FCSTD DOCUMENT  (FreeCAD 0.15R4403 (Git))
Label: logo
License: CC-BY 3.0
LicenseURL: http://creativecommons.org/licenses/by/3.0/
objects: Sketcher::SketchObject×1
note: 1 computed .brp shape members not serialized (recipe doc carries the construction recipe); baked Part::Feature solids carry a one-line shape summary decoded from their .brp

FEATURE [Sketcher::SketchObject] Sketch
  sketch-geometry (10):
    g0: LineSegment StartX=0 StartY=0 StartZ=0 EndX=85 EndY=0 EndZ=0
    g1: LineSegment StartX=85 StartY=0 StartZ=0 EndX=85 EndY=-45.5005 EndZ=0
    g2: LineSegment StartX=36.5444 StartY=-85 StartZ=0 EndX=0 EndY=-85 EndZ=0
    g3: LineSegment StartX=0 StartY=-85 StartZ=0 EndX=0 EndY=0 EndZ=0
    g4: LineSegment StartX=36.5444 StartY=-85 StartZ=0 EndX=40.9753 EndY=-71.3631 EndZ=0
    g5: LineSegment StartX=40.9753 StartY=-71.3631 StartZ=0 EndX=5.37857 EndY=-45.5005 EndZ=0
    g6: LineSegment StartX=5.37857 StartY=-45.5005 StartZ=0 EndX=49.3786 EndY=-45.5005 EndZ=0
    g7: LineSegment StartX=49.3786 StartY=-45.5005 StartZ=0 EndX=62.9753 EndY=-3.65401 EndZ=0
    g8: LineSegment StartX=62.9753 StartY=-3.65401 StartZ=0 EndX=76.5721 EndY=-45.5005 EndZ=0
    g9: LineSegment StartX=76.5721 StartY=-45.5005 StartZ=0 EndX=85 EndY=-45.5005 EndZ=0
  constraints (29):
    c: Coincident(g0,g1)
    c: Coincident(g2,g3)
    c: Coincident(g3,g0)
    c: Horizontal(g0)
    c: Vertical(g3)
    c: Coincident(g4,g5)
    c: Coincident(g5,g6)
    c: Coincident(g6,g7)
    c: Coincident(g7,g8)
    c: Coincident(g8,g9)
    c: Equal(g5,g6)
    c: Equal(g6,g7)
    c: Equal(g7,g8)
    c: Angle(g7,g8) = 0.628319
    c: Angle(g7,g6) = 1.88496
    c: Angle(g5,g6) = 0.628319
    c: Angle(g5,g4) = 1.88496
    c: Angle(g9,g8) = 1.88496
    c: Horizontal(g6)
    c: DistanceX(g0) = 85
    c: DistanceY(g3) = 85
    c: Horizontal(g2)
    c: Coincident(g-1,g0)
    c: Vertical(g1)
    c: Distance(g5) = 44
    c: Coincident(g1,g9)
    c: Coincident(g2,g4)
    c: DistanceY(g1) = -45.5005
    c: DistanceX(g2) = -36.5444
